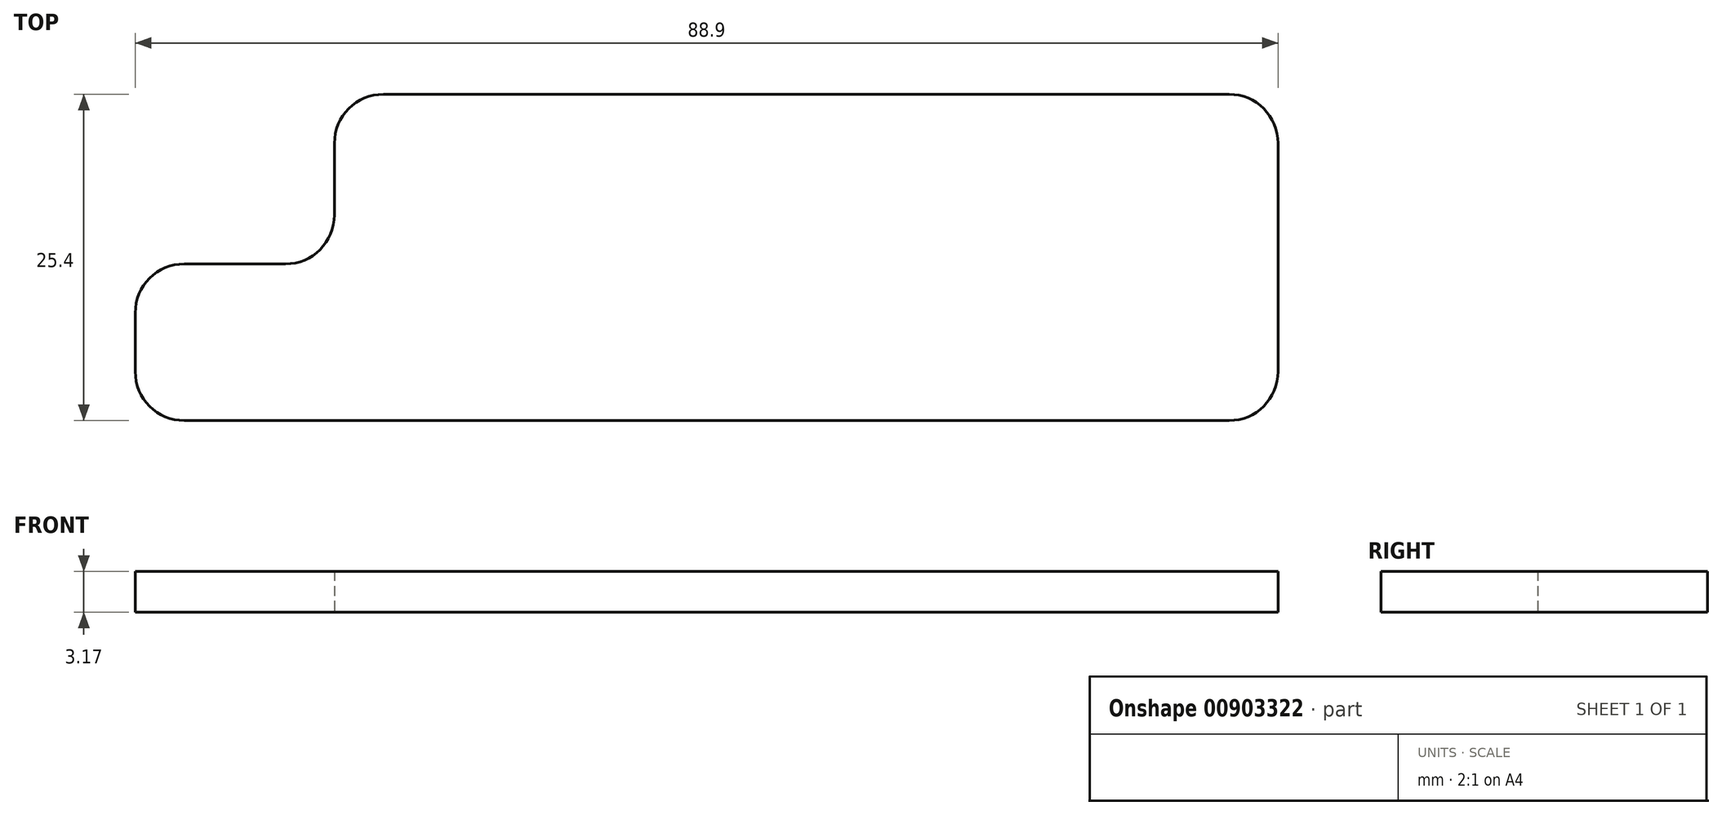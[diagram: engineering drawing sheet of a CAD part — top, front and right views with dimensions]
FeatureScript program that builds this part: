
annotation { "Feature Type Name" : "Feature", "Feature Type Description" : "" }
export const myFeature = defineFeature(function(context is Context, id is Id, definition is map)
    precondition{}
    {
        {
            var Q0;
            Q0=qCreatedBy(makeId("Top.planeOp"),FACE);
            var Q1;
            Q1=qCreatedBy(makeId("Front.planeOp"),FACE);
            var Q2;
            Q2=qCreatedBy(makeId("Top.planeOp"),FACE);
            var Q3;
            Q3=qCreatedBy(makeId("Top.planeOp"),FACE);
            var Q4;
            Q4=qCreatedBy(makeId("Top.planeOp"),FACE);
            var sketch = newSketch(context, id + "F0", { "sketchPlane" : qUnion([Q0, Q1, Q2, Q3, Q4])});
            skLineSegment(sketch, "E0.bottom", {"start": v(-15.24, 9.02) * mm, "end": v(50.55, 9.02) * mm});
            skLineSegment(sketch, "E0.top", {"start": v(-19.05, -16.38) * mm, "end": v(50.55, -16.38) * mm});
            skLineSegment(sketch, "E0.left", {"start": v(-19.05, 5.2) * mm, "end": v(-19.05, -0.38) * mm});
            skLineSegment(sketch, "E0.right", {"start": v(54.36, 5.2) * mm, "end": v(54.36, -12.57) * mm});
            skLineSegment(sketch, "E1.bottom", {"start": v(-19.05, -16.38) * mm, "end": v(-30.73, -16.38) * mm});
            skLineSegment(sketch, "E1.top", {"start": v(-22.86, -4.2) * mm, "end": v(-30.73, -4.2) * mm});
            skLineSegment(sketch, "E1.right", {"start": v(-34.54, -12.57) * mm, "end": v(-34.54, -8) * mm});
            skPoint(sketch, "E2.visualSharp", {"position": v(-19.05, 9.02) * mm});
            skArc(sketch, "E2.filletArc", {"start": v(-15.24, 9.02) * mm, "mid": v(-17.93, 7.9) * mm, "end": v(-19.05, 5.2) * mm});
            skPoint(sketch, "E3.visualSharp", {"position": v(54.36, 9.02) * mm});
            skArc(sketch, "E3.filletArc", {"start": v(54.36, 5.2) * mm, "mid": v(53.24, 7.9) * mm, "end": v(50.55, 9.02) * mm});
            skPoint(sketch, "E4.visualSharp", {"position": v(54.36, -16.38) * mm});
            skArc(sketch, "E4.filletArc", {"start": v(50.55, -16.38) * mm, "mid": v(53.24, -15.27) * mm, "end": v(54.36, -12.57) * mm});
            skPoint(sketch, "E5.visualSharp", {"position": v(-34.54, -16.38) * mm});
            skArc(sketch, "E5.filletArc", {"start": v(-34.54, -12.57) * mm, "mid": v(-33.43, -15.27) * mm, "end": v(-30.73, -16.38) * mm});
            skPoint(sketch, "E6.visualSharp", {"position": v(-34.54, -4.2) * mm});
            skArc(sketch, "E6.filletArc", {"start": v(-30.73, -4.2) * mm, "mid": v(-33.43, -5.3) * mm, "end": v(-34.54, -8) * mm});
            skPoint(sketch, "E7.visualSharp", {"position": v(-19.05, -4.2) * mm});
            skArc(sketch, "E7.filletArc", {"start": v(-22.86, -4.2) * mm, "mid": v(-20.17, -3.08) * mm, "end": v(-19.05, -0.38) * mm});
            skSolve(sketch);
        }
        {
            var Q0;
            Q0=makeQuery(id+"F0.imprint","IMPRINT",FACE,{"disambiguationData":[TD([[makeQuery(id+"F0.imprint","IMPRINT",EDGE,{"derivedFrom":sQuery(id+"F0.wireOp",EDGE,"E0.bottom")}),-1.0]])]});
            extrude(context, id + "F1", {"entities" : qUnion([Q0]), "depth" : 3.17 * mm, "offsetDistance" : 25.4 * mm});
        }
    });
